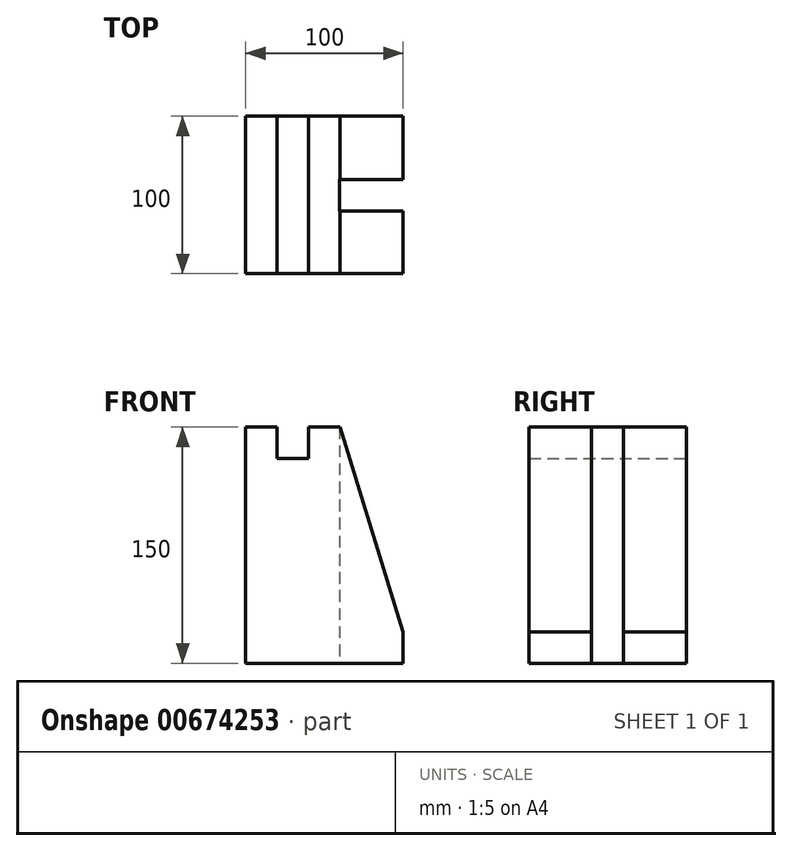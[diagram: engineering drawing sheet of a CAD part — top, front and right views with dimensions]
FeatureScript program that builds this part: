
annotation { "Feature Type Name" : "Feature", "Feature Type Description" : "" }
export const myFeature = defineFeature(function(context is Context, id is Id, definition is map)
    precondition{}
    {
        {
            var Q0;
            Q0=qCreatedBy(makeId("Front.planeOp"),FACE);
            var sketch = newSketch(context, id + "F0", { "sketchPlane" : qUnion([Q0])});
            skLineSegment(sketch, "E0", {"start": v(0, 0) * mm, "end": v(100, 0) * mm});
            skLineSegment(sketch, "E1", {"start": v(100, 0) * mm, "end": v(100, 20) * mm});
            skLineSegment(sketch, "E2", {"start": v(0, 0) * mm, "end": v(0, 150) * mm});
            skLineSegment(sketch, "E3", {"start": v(0, 150) * mm, "end": v(20, 150) * mm});
            skLineSegment(sketch, "E4", {"start": v(20, 150) * mm, "end": v(20, 130) * mm});
            skLineSegment(sketch, "E5", {"start": v(20, 130) * mm, "end": v(40, 130) * mm});
            skLineSegment(sketch, "E6", {"start": v(40, 130) * mm, "end": v(40, 150) * mm});
            skLineSegment(sketch, "E7", {"start": v(40, 150) * mm, "end": v(60, 150) * mm});
            skLineSegment(sketch, "E8", {"start": v(60, 150) * mm, "end": v(100, 20) * mm});
            skSolve(sketch);
        }
        {
            var Q0;
            Q0 = qSketchRegion(id + "F0", true);
            extrude(context, id + "F1", {"entities" : qUnion([Q0]), "depth" : 100 * mm, "offsetDistance" : 25 * mm});
        }
        {
            var Q0;
            Q0=makeQuery(id+"F1.opExtrude","SWEPT_FACE",FACE,{"disambiguationData":[OSD([sQuery(id+"F0.wireOp",EDGE,"E0")])]});
            var sketch = newSketch(context, id + "F2", { "sketchPlane" : qUnion([Q0])});
            skLineSegment(sketch, "E9", {"start": v(59.47, 100) * mm, "end": v(59.47, 0) * mm});
            skLineSegment(sketch, "E10", {"start": v(59.47, 40.19) * mm, "end": v(100, 40.19) * mm});
            skLineSegment(sketch, "E11", {"start": v(59.47, 60.3) * mm, "end": v(100, 60.3) * mm});
            skSolve(sketch);
        }
        {
            var Q0;
            Q0 = qSketchRegion(id + "F2", true);
            var Q1;
            {var subQ0=sQuery(id+"F2.wireOp",EDGE,"E10");Q1=makeQuery(id+"F2.imprint","IMPRINT",FACE,{"disambiguationData":[TD([[makeQuery(id+"F2.imprint","IMPRINT",EDGE,{"derivedFrom":subQ0}),1.0]])]});}
            extrude(context, id + "F3", {"entities" : qUnion([Q0, Q1]), "operationType" : NewBodyOperationType.REMOVE, "oppositeDirection" : true, "depth" : 100 * mm, "offsetDistance" : 25 * mm});
        }
        {
            var Q0;
            Q0=makeQuery(id+"F3.boolean.opBoolean","COPY",FACE,{"derivedFrom":makeQuery(id+"F3.opExtrude","CAP_FACE",FACE,{"disambiguationData":[OSD([sQuery(id+"F0.wireOp",EDGE,"E0"),sQuery(id+"F0.wireOp",EDGE,"E1"),sQuery(id+"F2.wireOp",EDGE,"E9"),sQuery(id+"F2.wireOp",EDGE,"E10"),sQuery(id+"F2.wireOp",EDGE,"E11")])],"isStart":false})});
            extrude(context, id + "F4", {"entities" : qUnion([Q0]), "operationType" : NewBodyOperationType.REMOVE, "oppositeDirection" : true, "depth" : 100 * mm, "offsetDistance" : 25 * mm});
        }
    });
